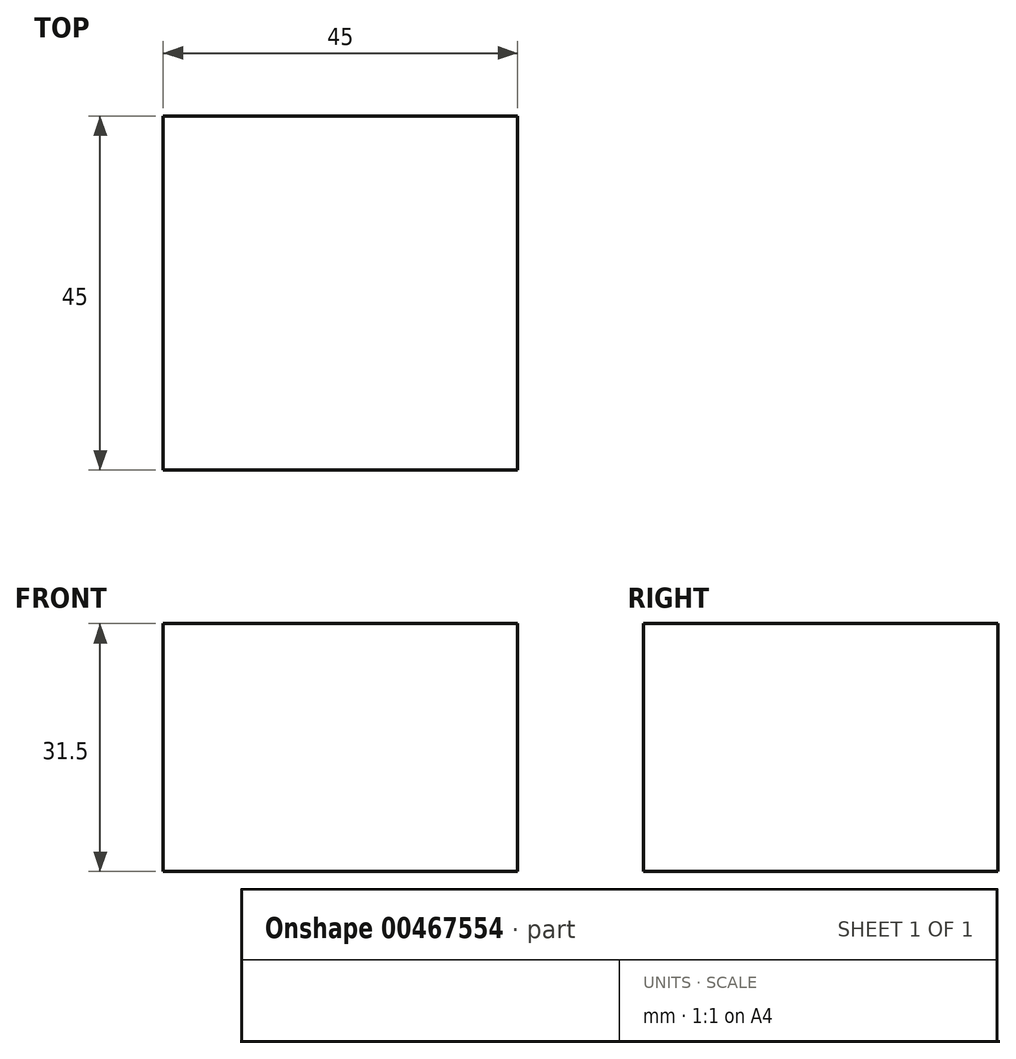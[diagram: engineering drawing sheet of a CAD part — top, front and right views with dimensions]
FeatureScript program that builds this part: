
annotation { "Feature Type Name" : "Feature", "Feature Type Description" : "" }
export const myFeature = defineFeature(function(context is Context, id is Id, definition is map)
    precondition{}
    {
        {
            var Q0;
            Q0=qCreatedBy(makeId("Top.planeOp"),FACE);
            var sketch = newSketch(context, id + "F0", { "sketchPlane" : qUnion([Q0])});
            skLineSegment(sketch, "E0.bottom", {"start": v(0, 0) * mm, "end": v(45, 0) * mm});
            skLineSegment(sketch, "E0.top", {"start": v(0, 45) * mm, "end": v(45, 45) * mm});
            skLineSegment(sketch, "E0.left", {"start": v(0, 0) * mm, "end": v(0, 45) * mm});
            skLineSegment(sketch, "E0.right", {"start": v(45, 0) * mm, "end": v(45, 45) * mm});
            skSolve(sketch);
        }
        {
            var Q0;
            Q0=qSketchRegion(id+"F0",true);
            extrude(context, id + "F1", {"entities" : qUnion([Q0]), "depth" : 15 * 2.1 * mm});
        }
    });
